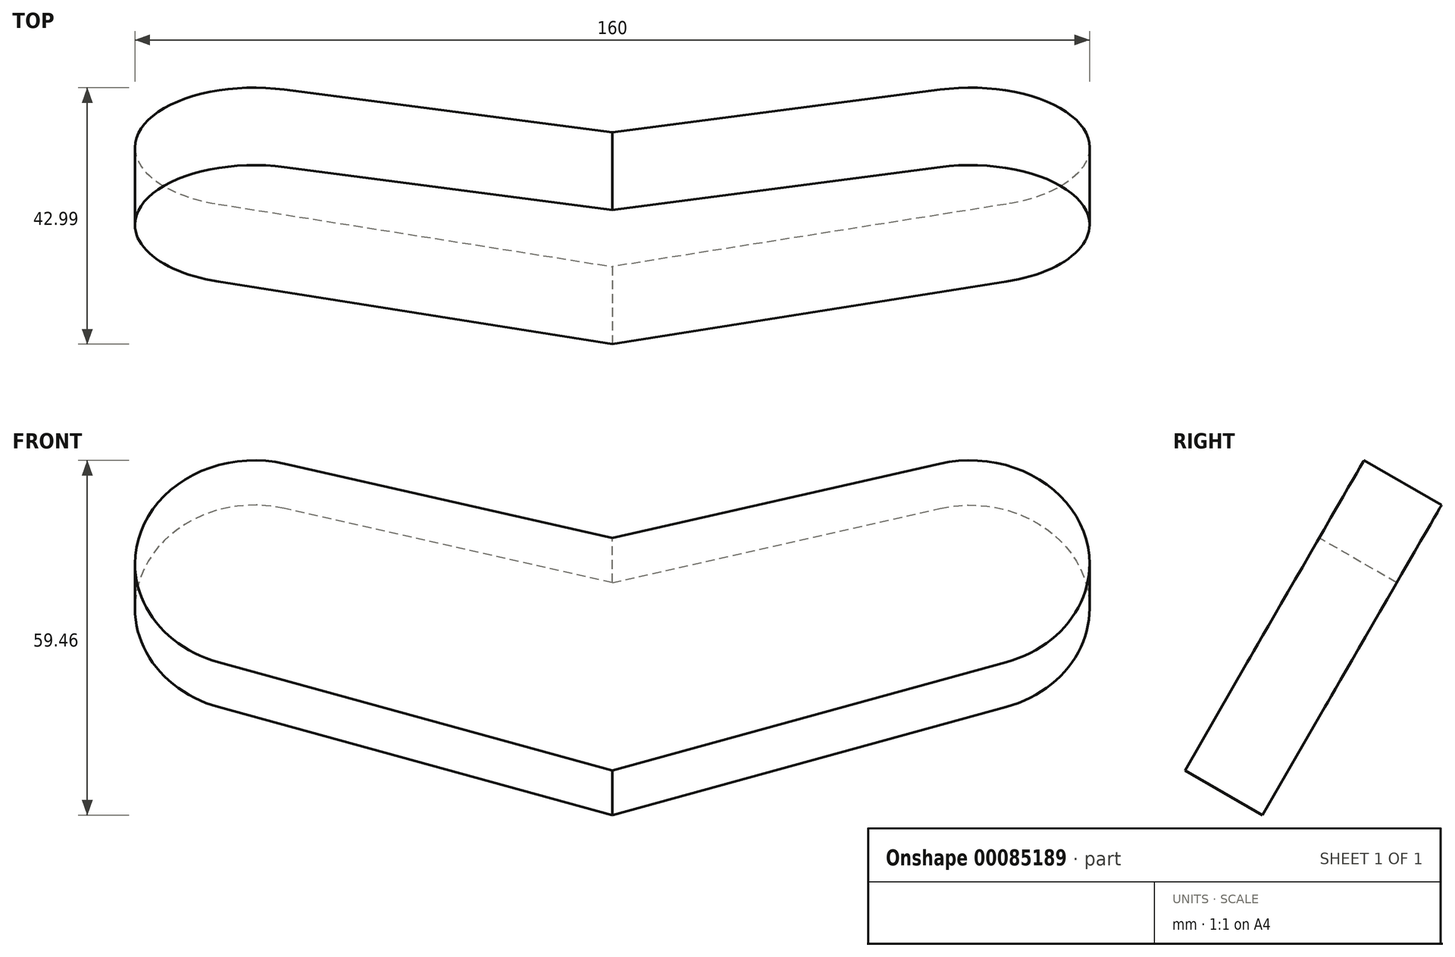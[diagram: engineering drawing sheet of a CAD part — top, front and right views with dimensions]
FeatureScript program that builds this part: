
annotation { "Feature Type Name" : "Feature", "Feature Type Description" : "" }
export const myFeature = defineFeature(function(context is Context, id is Id, definition is map)
    precondition{}
    {
        {
            var Q0;
            Q0=qCreatedBy(makeId("Front.planeOp"),FACE);
            var sketch = newSketch(context, id + "F0", { "sketchPlane" : qUnion([Q0])});
            skLineSegment(sketch, "E0", {"start": v(121.5, 0) * mm, "end": v(-118.02, 0) * mm, "construction": true});
            skSolve(sketch);
        }
        {
            var Q0;
            Q0=qCreatedBy(makeId("Front.planeOp"),FACE);
            var Q1;
            Q1=sQuery(id+"F0.wireOp",EDGE,"E0");
            cPlane(context, id + "F1", {"entities" : qUnion([Q0, Q1]), "cplaneType" : CPlaneType.LINE_ANGLE, "offset" : 150 * mm, "angle" : 30 * degree, "width" : 150 * mm, "height" : 150 * mm});
        }
        {
            var Q0;
            Q0=qCreatedBy(id+"F1.planeOp",FACE);
            cPlane(context, id + "F2", {"entities" : qUnion([Q0]), "cplaneType" : CPlaneType.OFFSET, "offset" : 5 * mm, "oppositeDirection" : true, "width" : 150 * mm, "height" : 150 * mm});
        }
        {
            var Q0;
            Q0=qCreatedBy(id+"F2.planeOp",FACE);
            var sketch = newSketch(context, id + "F3", { "sketchPlane" : qUnion([Q0])});
            skPoint(sketch, "E1", {"position": v(-60, 10) * mm});
            skArc(sketch, "E2", {"start": v(-54.95, 29.35) * mm, "mid": v(-79.21, 15.55) * mm, "end": v(-66.04, -9.07) * mm});
            skLineSegment(sketch, "E3", {"start": v(-66.04, -9.07) * mm, "end": v(0, -30) * mm});
            skLineSegment(sketch, "E4", {"start": v(0, -30) * mm, "end": v(0, 15) * mm});
            skLineSegment(sketch, "E5", {"start": v(0, 15) * mm, "end": v(-54.95, 29.35) * mm});
            skSolve(sketch);
        }
        {
            var Q0;
            Q0=makeQuery(id+"F3.imprint","IMPRINT",FACE,{"disambiguationData":[TD([[makeQuery(id+"F3.imprint","IMPRINT",EDGE,{"derivedFrom":sQuery(id+"F3.wireOp",EDGE,"E2")}),1.0]])]});
            extrude(context, id + "F4", {"entities" : qUnion([Q0]), "depth" : 15 * mm});
        }
        {
            var Q0;
            Q0=makeQuery(id+"F4.opExtrude","SWEPT_BODY",BODY,{"disambiguationData":[OSD([sQuery(id+"F3.wireOp",EDGE,"E2"),sQuery(id+"F3.wireOp",EDGE,"E3"),sQuery(id+"F3.wireOp",EDGE,"E4"),sQuery(id+"F3.wireOp",EDGE,"E5")])]});
            var Q1;
            Q1=qCreatedBy(makeId("Right.planeOp"),FACE);
            mirror(context, id + "F5", {"operationType" : NewBodyOperationType.ADD, "entities" : qUnion([Q0]), "mirrorPlane" : qUnion([Q1])});
        }
        {
            var Q0;
            Q0=makeQuery(id+"F4.opExtrude","SWEPT_BODY",BODY,{"disambiguationData":[OSD([sQuery(id+"F3.wireOp",EDGE,"E2"),sQuery(id+"F3.wireOp",EDGE,"E3"),sQuery(id+"F3.wireOp",EDGE,"E4"),sQuery(id+"F3.wireOp",EDGE,"E5")])]});
            transform(context, id + "F6", {"entities" : qUnion([Q0]), "transformType" : TransformType.TRANSLATION_3D, "dx" : 0 * mm, "dy" : 0 * mm, "dz" : 0 * mm, "makeCopy" : true});
        }
    });
